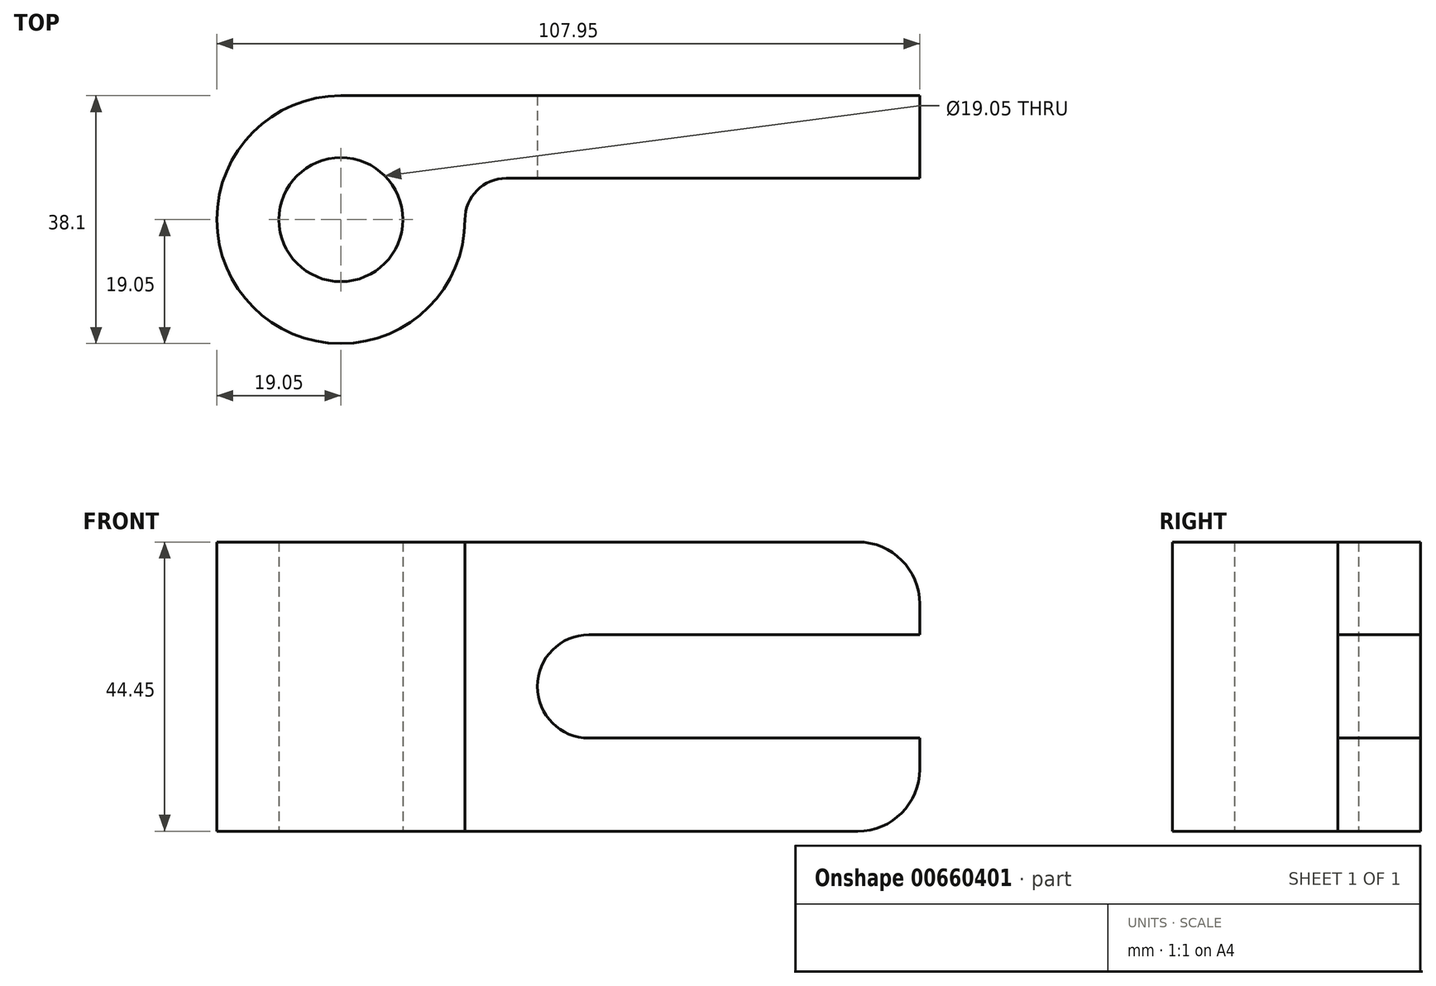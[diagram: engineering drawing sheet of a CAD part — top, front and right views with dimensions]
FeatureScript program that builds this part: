
annotation { "Feature Type Name" : "Feature", "Feature Type Description" : "" }
export const myFeature = defineFeature(function(context is Context, id is Id, definition is map)
    precondition{}
    {
        {
            var Q0;
            Q0=qCreatedBy(makeId("Top.planeOp"),FACE);
            var sketch = newSketch(context, id + "F0", { "sketchPlane" : qUnion([Q0])});
            skLineSegment(sketch, "E0", {"start": v(0, 0) * mm, "end": v(0, -19.05) * mm});
            skCircle(sketch, "E1", {"center": v(0, -19.05) * mm, "radius": 19.05 * mm});
            skCircle(sketch, "E2", {"center": v(0, -19.05) * mm, "radius": 9.53 * mm});
            skLineSegment(sketch, "E3.bottom", {"start": v(0, 0) * mm, "end": v(88.9, 0) * mm});
            skLineSegment(sketch, "E3.top", {"start": v(7.1, -12.7) * mm, "end": v(88.9, -12.7) * mm});
            skLineSegment(sketch, "E3.left", {"start": v(0, 0) * mm, "end": v(0, -12.7) * mm});
            skLineSegment(sketch, "E3.right", {"start": v(88.9, 0) * mm, "end": v(88.9, -12.7) * mm});
            skLineSegment(sketch, "E4", {"start": v(0, -19.05) * mm, "end": v(19.05, -19.05) * mm});
            skLineSegment(sketch, "E5", {"start": v(19.05, -19.05) * mm, "end": v(19.05, 0) * mm});
            skArc(sketch, "E6", {"start": v(25.4, -12.7) * mm, "mid": v(20.9, -14.56) * mm, "end": v(19.05, -19.05) * mm});
            skPoint(sketch, "E6.second.point", {"position": v(31.75, -19.05) * mm});
            skPoint(sketch, "E6.third.point", {"position": v(29.47, -23.92) * mm});
            skPoint(sketch, "E7", {"position": v(25.4, -12.7) * mm});
            skSolve(sketch);
        }
        {
            var Q0;
            {var subQ3=sQuery(id+"F0.wireOp",EDGE,"E4");var subQ5=sQuery(id+"F0.wireOp",EDGE,"E2");var subQ6=makeQuery(id+"F0.imprint","INTERSECT",VERTEX,{"derivedFrom":[subQ5,subQ3]});Q0=makeQuery(id+"F0.imprint","IMPRINT",FACE,{"disambiguationData":[TD([[makeQuery(id+"F0.imprint","IMPRINT",EDGE,{"disambiguationData":[TD([[subQ6,1.0]])],"derivedFrom":subQ5}),-1.0]])]});}
            var Q1;
            {var subQ3=sQuery(id+"F0.wireOp",EDGE,"E3.top");var subQ5=sQuery(id+"F0.wireOp",EDGE,"E2");var subQ7=makeQuery(id+"F0.imprint","INTERSECT",VERTEX,{"derivedFrom":[subQ5,subQ3]});Q1=makeQuery(id+"F0.imprint","IMPRINT",FACE,{"disambiguationData":[TD([[makeQuery(id+"F0.imprint","IMPRINT",EDGE,{"disambiguationData":[TD([[subQ7,1.0]])],"derivedFrom":subQ5}),-1.0]])]});}
            var Q2;
            {var subQ3=sQuery(id+"F0.wireOp",EDGE,"E3.top");var subQ5=sQuery(id+"F0.wireOp",EDGE,"E2");var subQ7=makeQuery(id+"F0.imprint","INTERSECT",VERTEX,{"derivedFrom":[subQ5,subQ3]});Q2=makeQuery(id+"F0.imprint","IMPRINT",FACE,{"disambiguationData":[TD([[makeQuery(id+"F0.imprint","IMPRINT",EDGE,{"disambiguationData":[TD([[subQ7,-1.0]])],"derivedFrom":subQ5}),-1.0]])]});}
            var Q3;
            {var subQ0=sQuery(id+"F0.wireOp",EDGE,"E3.right");Q3=makeQuery(id+"F0.imprint","IMPRINT",FACE,{"disambiguationData":[TD([[makeQuery(id+"F0.imprint","IMPRINT",EDGE,{"derivedFrom":subQ0}),-1.0]])]});}
            var Q4;
            {var subQ3=sQuery(id+"F0.wireOp",EDGE,"E3.top");var subQ5=sQuery(id+"F0.wireOp",EDGE,"E5");var subQ7=makeQuery(id+"F0.imprint","INTERSECT",VERTEX,{"derivedFrom":[subQ3,subQ5]});Q4=makeQuery(id+"F0.imprint","IMPRINT",FACE,{"disambiguationData":[TD([[makeQuery(id+"F0.imprint","IMPRINT",EDGE,{"disambiguationData":[TD([[subQ7,1.0]])],"derivedFrom":subQ3}),1.0]])]});}
            var Q5;
            {var subQ0=sQuery(id+"F0.wireOp",EDGE,"E5");var subQ3=sQuery(id+"F0.wireOp",EDGE,"E3.top");var subQ5=makeQuery(id+"F0.imprint","INTERSECT",VERTEX,{"derivedFrom":[subQ3,subQ0]});Q5=makeQuery(id+"F0.imprint","IMPRINT",FACE,{"disambiguationData":[TD([[makeQuery(id+"F0.imprint","IMPRINT",EDGE,{"disambiguationData":[TD([[subQ5,1.0]])],"derivedFrom":subQ3}),-1.0]])]});}
            var Q6;
            {var subQ0=sQuery(id+"F0.wireOp",EDGE,"E6");Q6=makeQuery(id+"F0.imprint","IMPRINT",FACE,{"disambiguationData":[TD([[makeQuery(id+"F0.imprint","IMPRINT",EDGE,{"derivedFrom":subQ0}),-1.0]])]});}
            extrude(context, id + "F1", {"entities" : qUnion([Q0, Q1, Q2, Q3, Q4, Q5, Q6]), "depth" : 44.45 * mm, "offsetDistance" : 25.4 * mm});
        }
        {
            var Q0;
            Q0=makeQuery(id+"F1.opExtrude","SWEPT_FACE",FACE,{"disambiguationData":[OSD([sQuery(id+"F0.wireOp",EDGE,"E3.top")])]});
            var sketch = newSketch(context, id + "F2", { "sketchPlane" : qUnion([Q0])});
            skLineSegment(sketch, "E8", {"start": v(79.38, 0) * mm, "end": v(38.1, 0) * mm});
            skArc(sketch, "E9", {"start": v(38.1, 30.18) * mm, "mid": v(30.16, 22.24) * mm, "end": v(38.1, 14.3) * mm});
            skLineSegment(sketch, "E10.top", {"start": v(38.1, 30.18) * mm, "end": v(88.9, 30.18) * mm});
            skLineSegment(sketch, "E10.right", {"start": v(88.9, 22.24) * mm, "end": v(88.9, 30.18) * mm});
            skLineSegment(sketch, "E11.top", {"start": v(38.1, 14.3) * mm, "end": v(88.9, 14.3) * mm});
            skLineSegment(sketch, "E11.right", {"start": v(88.9, 22.24) * mm, "end": v(88.9, 14.3) * mm});
            skPoint(sketch, "E12", {"position": v(88.9, 44.45) * mm});
            skLineSegment(sketch, "E13", {"start": v(88.9, 30.18) * mm, "end": v(88.9, 34.93) * mm});
            skLineSegment(sketch, "E14", {"start": v(79.38, 44.45) * mm, "end": v(75.56, 44.45) * mm});
            skArc(sketch, "E15.filletArc", {"start": v(88.9, 34.93) * mm, "mid": v(86.11, 41.66) * mm, "end": v(79.38, 44.45) * mm});
            skLineSegment(sketch, "E16", {"start": v(88.9, 14.3) * mm, "end": v(88.9, 0) * mm});
            skLineSegment(sketch, "E17", {"start": v(88.9, 0) * mm, "end": v(69.1, 0) * mm});
            skPoint(sketch, "E18", {"position": v(88.9, 0) * mm});
            skLineSegment(sketch, "E19", {"start": v(88.9, 14.3) * mm, "end": v(88.9, 9.53) * mm});
            skLineSegment(sketch, "E20", {"start": v(69.1, 0) * mm, "end": v(88.9, 0) * mm});
            skArc(sketch, "E21.filletArc", {"start": v(79.38, 0) * mm, "mid": v(86.11, 2.79) * mm, "end": v(88.9, 9.53) * mm});
            skSolve(sketch);
        }
        {
            var Q0;
            Q0=makeQuery(id+"F2.imprint","IMPRINT",FACE,{"disambiguationData":[TD([[makeQuery(id+"F2.imprint","IMPRINT",EDGE,{"derivedFrom":sQuery(id+"F2.wireOp",EDGE,"E9")}),1.0]])]});
            var Q1;
            {var subQ0=sQuery(id+"F2.wireOp",EDGE,"E15.filletArc");Q1=makeQuery(id+"F2.imprint","IMPRINT",FACE,{"disambiguationData":[TD([[makeQuery(id+"F2.imprint","IMPRINT",EDGE,{"derivedFrom":subQ0}),-1.0]])]});}
            var Q2;
            {var subQ0=sQuery(id+"F2.wireOp",EDGE,"E16");Q2=makeQuery(id+"F2.imprint","IMPRINT",FACE,{"disambiguationData":[TD([[makeQuery(id+"F2.imprint","IMPRINT",EDGE,{"derivedFrom":subQ0}),-1.0]])]});}
            extrude(context, id + "F3", {"entities" : qUnion([Q0, Q1, Q2]), "operationType" : NewBodyOperationType.REMOVE, "endBound" : BoundingType.THROUGH_ALL, "oppositeDirection" : true, "depth" : 25.4 * mm, "offsetDistance" : 25.4 * mm});
        }
    });
